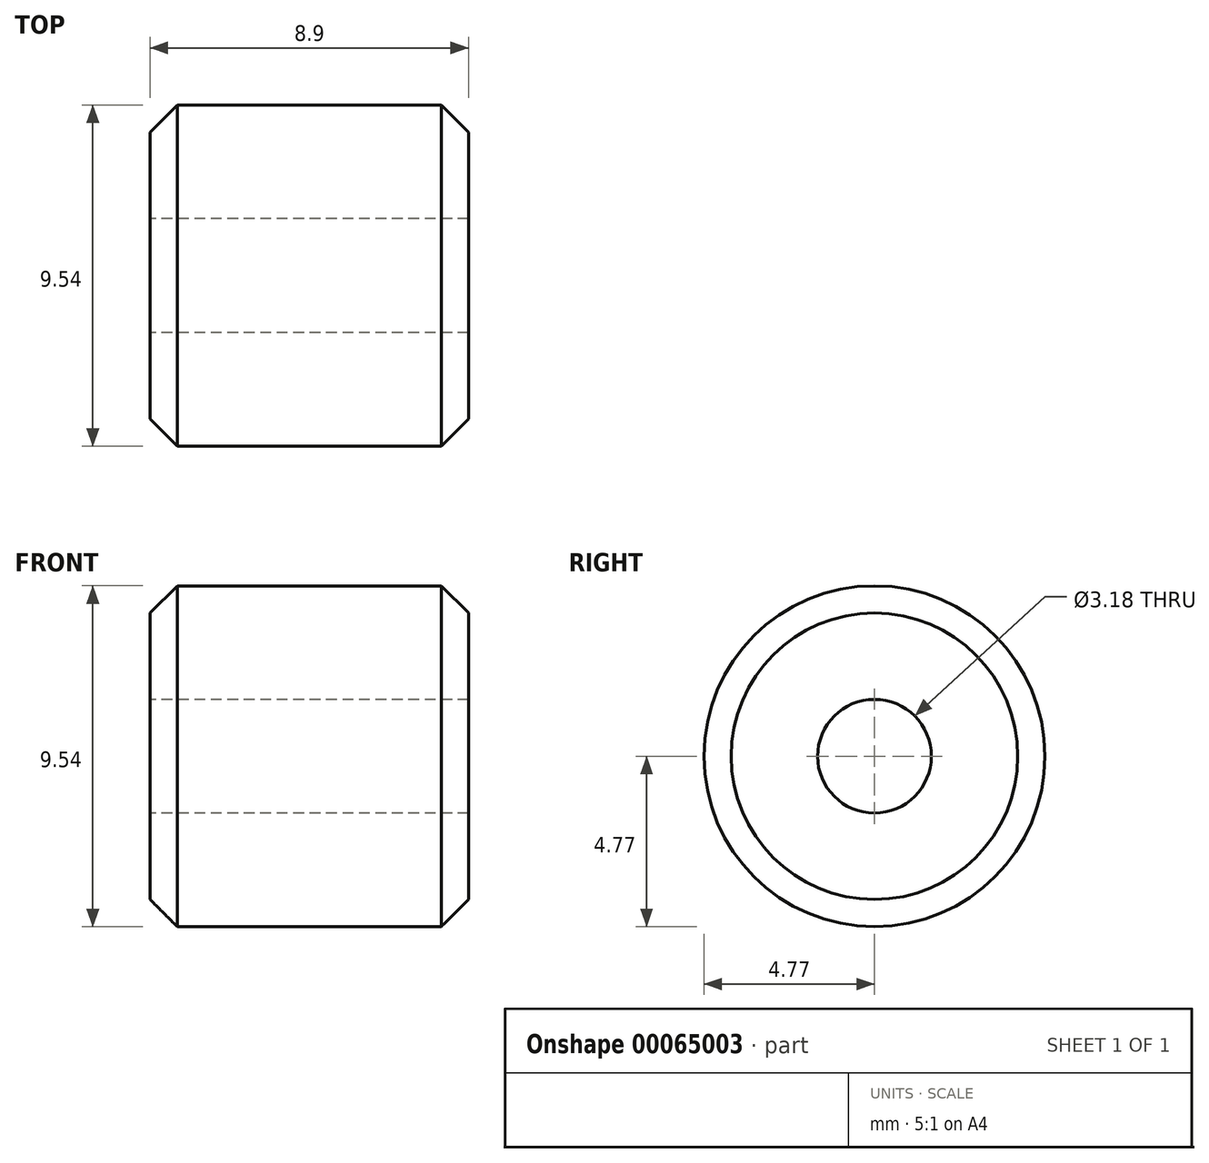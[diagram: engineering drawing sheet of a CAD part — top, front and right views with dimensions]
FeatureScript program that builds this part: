
annotation { "Feature Type Name" : "Feature", "Feature Type Description" : "" }
export const myFeature = defineFeature(function(context is Context, id is Id, definition is map)
    precondition{}
    {
        {
            var Q0;
            Q0=qCreatedBy(makeId("Right.planeOp"),FACE);
            var sketch = newSketch(context, id + "F0", { "sketchPlane" : qUnion([Q0])});
            skCircle(sketch, "E0", {"center": v(0, 0) * mm, "radius": 4.77 * mm});
            skCircle(sketch, "E1", {"center": v(0, 0) * mm, "radius": 1.6 * mm});
            skSolve(sketch);
        }
        {
            var Q0;
            Q0 = qSketchRegion(id + "F0", true);
            extrude(context, id + "F1", {"entities" : qUnion([Q0]), "endBound" : BoundingType.SYMMETRIC, "depth" : 8.9 * mm});
        }
        {
            var Q0;
            Q0=makeQuery(id+"F1.opExtrude","SWEPT_FACE",FACE,{"disambiguationData":[OSD([sQuery(id+"F0.wireOp",EDGE,"E0")])]});
            chamfer(context, id + "F2", {"entities" : qUnion([Q0]), "width" : 0.76 * mm, "tangentPropagation" : true});
        }
    });
